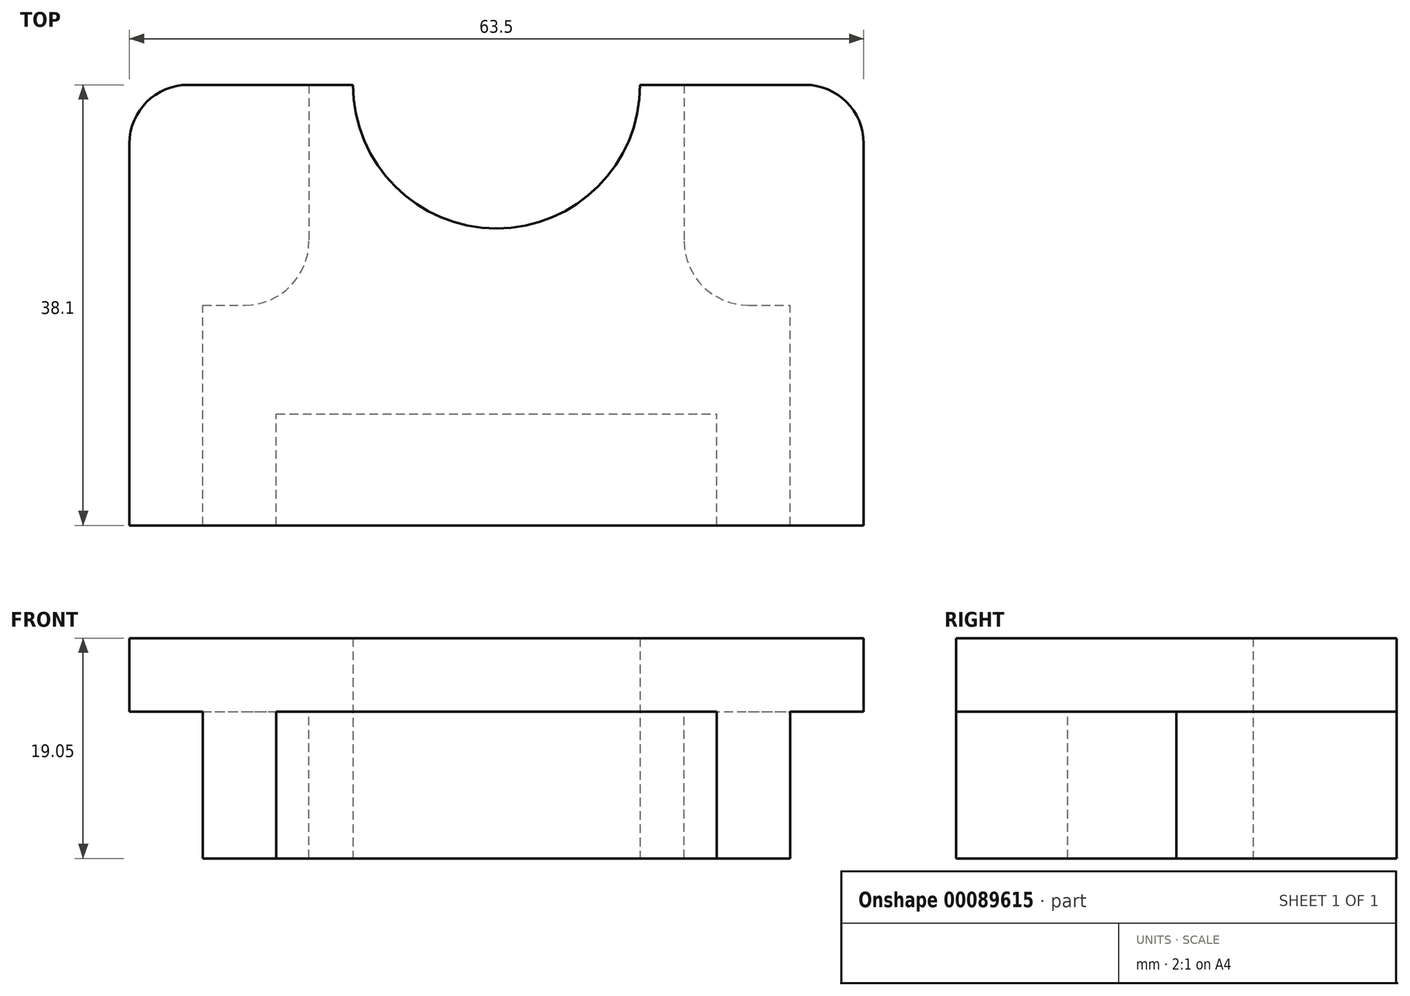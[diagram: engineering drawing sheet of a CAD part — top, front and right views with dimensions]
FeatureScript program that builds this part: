
annotation { "Feature Type Name" : "Feature", "Feature Type Description" : "" }
export const myFeature = defineFeature(function(context is Context, id is Id, definition is map)
    precondition{}
    {
        {
            var Q0;
            Q0=qCreatedBy(makeId("Top.planeOp"),FACE);
            var sketch = newSketch(context, id + "F0", { "sketchPlane" : qUnion([Q0])});
            skLineSegment(sketch, "E0.bottom", {"start": v(-31.75, 19.05) * mm, "end": v(-12.42, 19.05) * mm});
            skLineSegment(sketch, "E0.top", {"start": v(-31.75, -19.05) * mm, "end": v(31.75, -19.05) * mm});
            skLineSegment(sketch, "E0.left", {"start": v(-31.75, 19.05) * mm, "end": v(-31.75, -19.05) * mm});
            skLineSegment(sketch, "E0.right", {"start": v(31.75, 19.05) * mm, "end": v(31.75, -19.05) * mm});
            skArc(sketch, "E1", {"start": v(-12.42, 19.05) * mm, "mid": v(0, 6.63) * mm, "end": v(12.42, 19.05) * mm});
            skLineSegment(sketch, "E2.trimOffspring", {"start": v(12.42, 19.05) * mm, "end": v(31.75, 19.05) * mm});
            skSolve(sketch);
        }
        {
            var Q0;
            Q0=makeQuery(id+"F0.imprint","IMPRINT",FACE,{"disambiguationData":[TD([[makeQuery(id+"F0.imprint","IMPRINT",EDGE,{"derivedFrom":sQuery(id+"F0.wireOp",EDGE,"E0.bottom")}),-1.0]])]});
            extrude(context, id + "F1", {"entities" : qUnion([Q0]), "depth" : 6.35 * mm});
        }
        {
            var Q0;
            Q0=qCreatedBy(makeId("Top.planeOp"),FACE);
            var sketch = newSketch(context, id + "F2", { "sketchPlane" : qUnion([Q0])});
            skLineSegment(sketch, "E3.0.0", {"start": v(-31.75, 19.05) * mm, "end": v(-12.42, 19.05) * mm});
            skArc(sketch, "E3.0.1", {"start": v(-12.42, 19.05) * mm, "mid": v(0, 6.63) * mm, "end": v(12.42, 19.05) * mm});
            skLineSegment(sketch, "E3.0.2", {"start": v(12.42, 19.05) * mm, "end": v(31.75, 19.05) * mm});
            skLineSegment(sketch, "E3.0.3", {"start": v(31.75, 19.05) * mm, "end": v(31.75, -19.05) * mm});
            skLineSegment(sketch, "E3.0.4", {"start": v(31.75, -19.05) * mm, "end": v(-31.75, -19.05) * mm});
            skLineSegment(sketch, "E3.0.5", {"start": v(-31.75, -19.05) * mm, "end": v(-31.75, 19.05) * mm});
            skLineSegment(sketch, "E4.bottom", {"start": v(-25.4, -19.05) * mm, "end": v(25.4, -19.05) * mm});
            skLineSegment(sketch, "E4.top", {"start": v(-25.4, 19.05) * mm, "end": v(25.4, 19.05) * mm});
            skLineSegment(sketch, "E4.left", {"start": v(-25.4, -19.05) * mm, "end": v(-25.4, 19.05) * mm});
            skLineSegment(sketch, "E4.right", {"start": v(25.4, -19.05) * mm, "end": v(25.4, 19.05) * mm});
            skLineSegment(sketch, "E5.bottom", {"start": v(-19.05, -19.05) * mm, "end": v(19.05, -19.05) * mm});
            skLineSegment(sketch, "E5.top", {"start": v(-19.05, -9.4) * mm, "end": v(19.05, -9.4) * mm});
            skLineSegment(sketch, "E5.left", {"start": v(-19.05, -19.05) * mm, "end": v(-19.05, -9.4) * mm});
            skLineSegment(sketch, "E5.right", {"start": v(19.05, -19.05) * mm, "end": v(19.05, -9.4) * mm});
            skLineSegment(sketch, "E6", {"start": v(-16.23, 19.05) * mm, "end": v(-16.23, 0) * mm});
            skLineSegment(sketch, "E7", {"start": v(0, 44.47) * mm, "end": v(0, -44.69) * mm, "construction": true});
            skLineSegment(sketch, "E8.MirrorCS", {"start": v(16.23, 19.05) * mm, "end": v(16.23, 0) * mm});
            skLineSegment(sketch, "E9", {"start": v(-25.4, 0) * mm, "end": v(-16.23, 0) * mm});
            skLineSegment(sketch, "E10", {"start": v(16.23, 0) * mm, "end": v(25.4, 0) * mm});
            skSolve(sketch);
        }
        {
            var Q0;
            {var subQ1=sQuery(id+"F2.wireOp",EDGE,"E3.0.1");Q0=makeQuery(id+"F2.imprint","IMPRINT",FACE,{"disambiguationData":[TD([[makeQuery(id+"F2.imprint","IMPRINT",EDGE,{"derivedFrom":subQ1}),-1.0]])]});}
            extrude(context, id + "F3", {"entities" : qUnion([Q0]), "operationType" : NewBodyOperationType.ADD, "oppositeDirection" : true, "depth" : 12.7 * mm});
        }
        {
            var Q0;
            Q0=makeQuery(id+"F3.opExtrude","SWEPT_EDGE",EDGE,{"disambiguationData":[OSD([sQuery(id+"F2.wireOp",EDGE,"E8.MirrorCS"),sQuery(id+"F2.wireOp",EDGE,"E10")])]});
            var Q1;
            Q1=makeQuery(id+"F3.opExtrude","SWEPT_EDGE",EDGE,{"disambiguationData":[OSD([sQuery(id+"F2.wireOp",EDGE,"E6"),sQuery(id+"F2.wireOp",EDGE,"E9")])]});
            fillet(context, id + "F4", {"entities" : qUnion([Q0, Q1]), "radius" : 5.54 * mm, "tangentPropagation" : true, "allowEdgeOverflow" : false});
        }
        {
            var Q0;
            Q0=makeQuery(id+"F1.opExtrude","SWEPT_EDGE",EDGE,{"disambiguationData":[OSD([sQuery(id+"F0.wireOp",EDGE,"E0.right"),sQuery(id+"F0.wireOp",EDGE,"E2.trimOffspring")])]});
            var Q1;
            Q1=makeQuery(id+"F1.opExtrude","SWEPT_EDGE",EDGE,{"disambiguationData":[OSD([sQuery(id+"F0.wireOp",EDGE,"E0.bottom"),sQuery(id+"F0.wireOp",EDGE,"E0.left")])]});
            fillet(context, id + "F5", {"entities" : qUnion([Q0, Q1]), "radius" : 5.08 * mm, "tangentPropagation" : true, "allowEdgeOverflow" : false});
        }
    });
